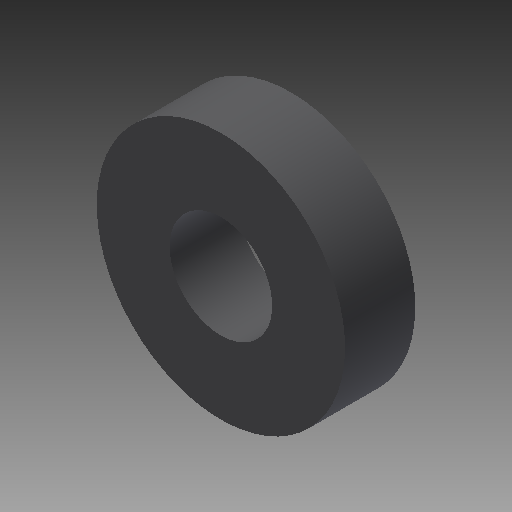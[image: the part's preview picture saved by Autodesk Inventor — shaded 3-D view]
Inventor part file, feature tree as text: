
AUTODESK INVENTOR PART (.ipt)
format: ipt  version: 2017 (Build 210142000, 142)  size: 100,352 bytes
history: native  units: in
note: dims shown in document units (in); Inventor stores cm internally (conversion verified against a paired STEP export)
features: other x7, revolve x1, sketch x1
ambient origin geometry x8: Origin, YZ Plane, XZ Plane, XY Plane, X Axis, Y Axis, Z Axis, Center Point
bodies: Solid1 (feature_tree)
feature tree (9):
  revolve  "Revolution1"  [1 undecoded]
  other  "part_to_rod_XY"
  other  "part_to_rod_YZ"
  other  "part_to_rod_ZX"
  other  "part_to_rod_X"
  other  "part_to_rod_Y"
  other  "part_to_rod_Z"
  other  "part_to_rod_Center"
  sketch  "Sketch_1"  dims[d0=360.0deg d1=0.0in]
note: 1 required parameter value undecoded (feature->parameter linkage not recoverable at this tier; creation-order binding heuristic only, values carry confidence <= 0.55)
